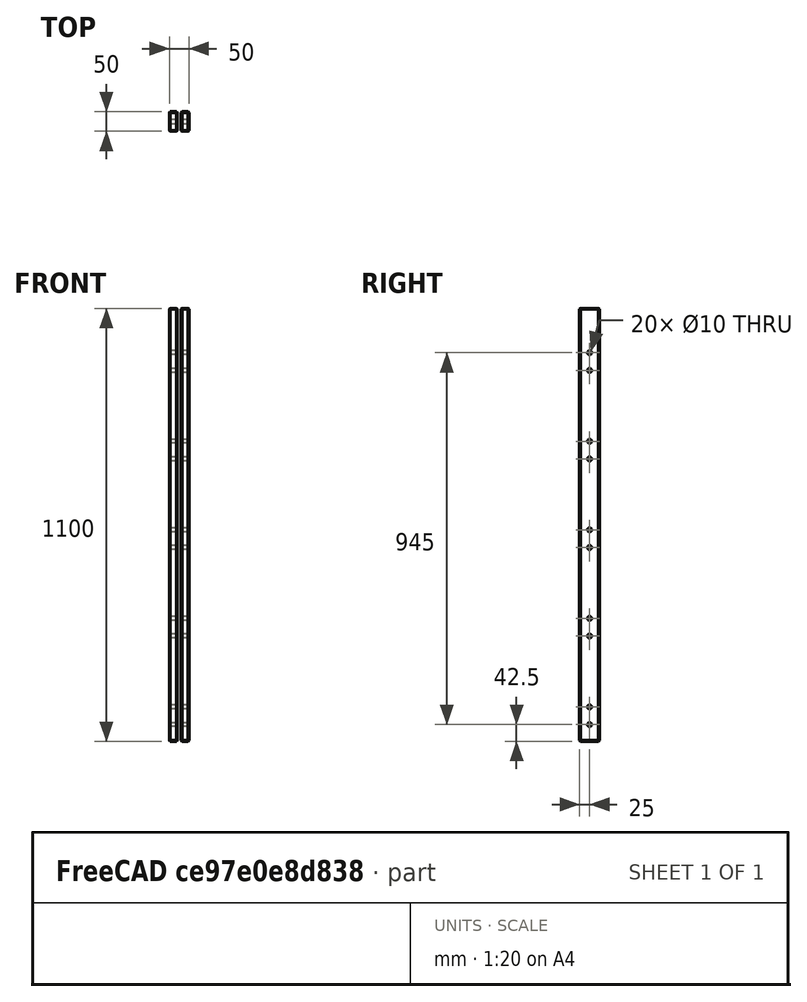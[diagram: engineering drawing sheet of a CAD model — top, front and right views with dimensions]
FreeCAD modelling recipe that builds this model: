
FCSTD DOCUMENT  (FreeCAD 0.17R10993 (Git))
Label: railing_wood
License: All rights reserved
LicenseURL: http://en.wikipedia.org/wiki/All_rights_reserved
objects: Part::Part2DObjectPython×22, Part::Feature×5, TechDraw::DrawProjGroupItem×3, Part::FeaturePython×2, Part::Box×1, Part::Mirroring×1, Part::Compound×1, Part::Chamfer×1, Part::Extrusion×1, Part::Cut×1, App::DocumentObjectGroup×1, TechDraw::DrawSVGTemplate×1, TechDraw::DrawProjGroup×1, TechDraw::DrawViewPart×1, TechDraw::DrawPage×1
note: 35 computed .brp shape members not serialized (recipe doc carries the construction recipe); baked Part::Feature solids carry a one-line shape summary decoded from their .brp

FEATURE [Part::Box] Box  label="Cube"
  AttacherType = Attacher::AttachEngine3D
  Height = 1100
  Length = 20
  Placement = pos=(-25,-23,-70) rot=(0,0,1;0rad)
  Width = 50
FEATURE [Part::Mirroring] mirror  label="Mirror of Cube"
  Base = (0,0,0)
  Normal = (1,0,0)
  Source = -> Box
FEATURE [Part::Compound] Compound
  Links = -> [mirror,Box]
  Placement = pos=(89.3902,-413,100) rot=(0,0,1;0rad)
FEATURE [Part::Chamfer] Chamfer  label="railing_wood"
  Base = -> Compound
  Edges = 24 edges r=2: [Edge1,Edge2,Edge3,Edge4,Edge5,Edge6,Edge7,Edge8,Edge9,Edge10,Edge11,Edge12,Edge13,Edge14,Edge15,Edge16,Edge17,Edge18,Edge19,Edge20,Edge21,Edge22,Edge23,Edge24]
FEATURE [Part::Feature] step_01_cs
  shape: bbox 1490 x 3e-07 x 1265 mm, 0 faces, 0 solids (baked)
FEATURE [Part::Feature] fridge_box_panels_01_cs
  shape: bbox 630 x 3e-07 x 2050 mm, 0 faces, 0 solids (baked)
FEATURE [Part::Part2DObjectPython] Line  # Draft 2D object (typed FeaturePython)
  ChamferSize = 0
  Closed = false
  End = (2100,-5,0)
  FilletRadius = 0
  Length = 2100.01
  MakeFace = true
  Points = (2) [(0,0,0),(2100,-5,0)]
  Start = (0,0,0)
  Subdivisions = 0
FEATURE [Part::Part2DObjectPython] Line002  # Draft 2D object (typed FeaturePython)
  ChamferSize = 0
  Closed = false
  End = (2900,0,2260)
  FilletRadius = 0
  Length = 800
  MakeFace = true
  Points = (2) [(2100,0,2260),(2900,0,2260)]
  Start = (2100,0,2260)
  Subdivisions = 0
FEATURE [Part::Part2DObjectPython] DWire  # Draft 2D object (typed FeaturePython)
  ChamferSize = 0
  Closed = false
  End = (2900,0,2105)
  FilletRadius = 0
  Length = 1755
  MakeFace = true
  Points = (4) [(2900,0,2260),(2100,0,2260),(2100,0,2105),(2900,0,2105)]
  Start = (2900,0,2260)
  Subdivisions = 0
FEATURE [Part::Part2DObjectPython] Line003  # Draft 2D object (typed FeaturePython)
  ChamferSize = 0
  Closed = false
  End = (2100,0,3260)
  FilletRadius = 0
  Length = 1000
  MakeFace = true
  Points = (2) [(2100,0,2260),(2100,0,3260)]
  Start = (2100,0,2260)
  Subdivisions = 0
FEATURE [Part::Part2DObjectPython] Line005  # Draft 2D object (typed FeaturePython)
  ChamferSize = 0
  Closed = false
  End = (0,0,1205)
  FilletRadius = 0
  Length = 1000
  MakeFace = true
  Points = (2) [(-1.18132e-16,0,205),(-1.18132e-16,0,1205)]
  Start = (0,0,205)
  Subdivisions = 0
FEATURE [Part::Part2DObjectPython] Line009  # Draft 2D object (typed FeaturePython)
  ChamferSize = 0
  Closed = false
  End = (89.3902,0,1222.39)
  FilletRadius = 0
  Length = 902.176
  MakeFace = true
  Placement = pos=(-630,0,-420.411) rot=(0,0,1;0rad)
  Points = (2) [(719.39,0,740.622),(719.39,0,1642.8)]
  Start = (89.3902,0,320.211)
  Subdivisions = 0
FEATURE [Part::Feature] double_beam_01_cs001
  Placement = pos=(0,365,0) rot=(0,0,1;0rad)
  shape: bbox 1510 x 3e-07 x 1687 mm, 0 faces, 0 solids (baked)
FEATURE [Part::Part2DObjectPython] Line016  # Draft 2D object (typed FeaturePython)
  ChamferSize = 0
  Closed = false
  End = (148.345,-431,590)
  FilletRadius = 0
  Length = 58.9552
  MakeFace = true
  Placement = pos=(2.73e-10,-431,59.7885) rot=(0,0,1;0rad)
  Points = (2) [(89.3902,0,530.211),(148.345,0,530.211)]
  Start = (89.3902,-431,590)
  Subdivisions = 0
FEATURE [Part::Part2DObjectPython] Line019  # Draft 2D object (typed FeaturePython)
  ChamferSize = 0
  Closed = false
  End = (148.345,-431,815)
  FilletRadius = 0
  Length = 58.9552
  MakeFace = true
  Placement = pos=(2.73e-10,-431,284.789) rot=(0,0,1;0rad)
  Points = (2) [(89.3902,0,530.211),(148.345,0,530.211)]
  Start = (89.3902,-431,815)
  Subdivisions = 0
FEATURE [Part::Part2DObjectPython] Line022  # Draft 2D object (typed FeaturePython)
  ChamferSize = 0
  Closed = false
  End = (1490,0,1687.47)
  FilletRadius = 0
  Length = 2110.19
  MakeFace = true
  Points = (2) [(-20,0,213.426),(1490,0,1687.47)]
  Start = (-20,0,213.426)
  Subdivisions = 0
FEATURE [Part::Part2DObjectPython] Line023  # Draft 2D object (typed FeaturePython)
  ChamferSize = 0
  Closed = false
  End = (1490,0,2659.52)
  FilletRadius = 0
  Length = 2110.19
  MakeFace = true
  Placement = pos=(0,0,972.05) rot=(0,0,1;0rad)
  Points = (2) [(-20,0,213.426),(1490,0,1687.47)]
  Start = (-20,0,1185.48)
  Subdivisions = 0
FEATURE [Part::Part2DObjectPython] Line024  # Draft 2D object (typed FeaturePython)
  ChamferSize = 0
  Closed = false
  End = (1524.93,0,2623.75)
  FilletRadius = 0
  Length = 2110.19
  MakeFace = true
  Points = (2) [(14.9268,0,1149.7),(1524.93,0,2623.75)]
  Start = (14.9268,0,1149.7)
  Subdivisions = 0
FEATURE [Part::Part2DObjectPython] Line026  # Draft 2D object (typed FeaturePython)
  ChamferSize = 0
  Closed = false
  End = (148.345,-431,1040)
  FilletRadius = 0
  Length = 58.9552
  MakeFace = true
  Placement = pos=(2.74e-10,-431,509.789) rot=(0,0,1;0rad)
  Points = (2) [(89.3902,0,530.211),(148.345,0,530.211)]
  Start = (89.3902,-431,1040)
  Subdivisions = 0
FEATURE [Part::Part2DObjectPython] Line033  # Draft 2D object (typed FeaturePython)
  ChamferSize = 0
  Closed = false
  End = (89.3902,-431,500)
  FilletRadius = 0
  Length = 58.9552
  MakeFace = true
  Placement = pos=(-58.9552,-431,-30.2115) rot=(0,0,1;0rad)
  Points = (2) [(89.3902,0,530.211),(148.345,0,530.211)]
  Start = (30.4351,-431,500)
  Subdivisions = 0
FEATURE [Part::Part2DObjectPython] Line034  # Draft 2D object (typed FeaturePython)
  ChamferSize = 0
  Closed = false
  End = (89.3902,-431,725)
  FilletRadius = 0
  Length = 58.9552
  MakeFace = true
  Placement = pos=(-58.9552,-431,194.789) rot=(0,0,1;0rad)
  Points = (2) [(89.3902,0,530.211),(148.345,0,530.211)]
  Start = (30.4351,-431,725)
  Subdivisions = 0
FEATURE [Part::Part2DObjectPython] Line035  # Draft 2D object (typed FeaturePython)
  ChamferSize = 0
  Closed = false
  End = (89.3902,-431,950)
  FilletRadius = 0
  Length = 58.9552
  MakeFace = true
  Placement = pos=(-58.9552,-431,419.789) rot=(0,0,1;0rad)
  Points = (2) [(89.3902,0,530.211),(148.345,0,530.211)]
  Start = (30.4351,-431,950)
  Subdivisions = 0
FEATURE [Part::Part2DObjectPython] Line036  # Draft 2D object (typed FeaturePython)
  ChamferSize = 0
  Closed = false
  End = (148.345,-431,365)
  FilletRadius = 0
  Length = 58.9552
  MakeFace = true
  Placement = pos=(2.73e-10,-431,-165.211) rot=(0,0,1;0rad)
  Points = (2) [(89.3902,0,530.211),(148.345,0,530.211)]
  Start = (89.3902,-431,365)
  Subdivisions = 0
FEATURE [Part::Part2DObjectPython] Line037  # Draft 2D object (typed FeaturePython)
  ChamferSize = 0
  Closed = false
  End = (89.3902,-431,275)
  FilletRadius = 0
  Length = 58.9552
  MakeFace = true
  Placement = pos=(-58.9552,-431,-255.211) rot=(0,0,1;0rad)
  Points = (2) [(89.3902,0,530.211),(148.345,0,530.211)]
  Start = (30.4351,-431,275)
  Subdivisions = 0
FEATURE [Part::Part2DObjectPython] Line038  # Draft 2D object (typed FeaturePython)
  ChamferSize = 0
  Closed = false
  End = (89.3902,-431,50)
  FilletRadius = 0
  Length = 58.9552
  MakeFace = true
  Placement = pos=(-58.9552,-431,-480.211) rot=(0,0,1;0rad)
  Points = (2) [(89.3902,0,530.211),(148.345,0,530.211)]
  Start = (30.4351,-431,50)
  Subdivisions = 0
FEATURE [Part::Part2DObjectPython] Line039  # Draft 2D object (typed FeaturePython)
  ChamferSize = 0
  Closed = false
  End = (148.345,-431,140)
  FilletRadius = 0
  Length = 58.9552
  MakeFace = true
  Placement = pos=(2.73e-10,-431,-390.211) rot=(0,0,1;0rad)
  Points = (2) [(89.3902,0,530.211),(148.345,0,530.211)]
  Start = (89.3902,-431,140)
  Subdivisions = 0
FEATURE [Part::Part2DObjectPython] Circle  # Draft 2D object (typed FeaturePython)
  FirstAngle = 0
  LastAngle = 0
  MakeFace = true
  Placement = pos=(64.3902,-411,100) rot=(0.57735,-0.57735,-0.57735;2.0944rad)
  Radius = 5
  Support = -> [Chamfer]
FEATURE [Part::Extrusion] Extrude
  Base = -> Circle
  Dir = (1,0,0)
  DirMode = 0
  FaceMakerClass = Part::FaceMakerBullseye
  LengthFwd = 80
  LengthRev = 0
  Placement = pos=(25,0,0) rot=(0,0,1;0rad)
  Solid = false
  Symmetric = true
FEATURE [Part::FeaturePython] Array  # Draft array (typed FeaturePython)
  Angle = 360
  ArrayType = 0
  Axis = (0,0,1)
  Base = -> Extrude
  Center = (0,0,0)
  Fuse = false
  IntervalAxis = (0,0,0)
  IntervalX = (0,0,45)
  IntervalY = (0,0,225)
  IntervalZ = (0,0,0)
  NumberPolar = 1
  NumberX = 2
  NumberY = 5
  NumberZ = 1
  Placement = pos=(0,0,-27.5) rot=(0,0,1;0rad)
FEATURE [Part::Cut] Cut  label="cutted_railing_wood"
  Base = -> Chamfer
  Tool = -> Array
FEATURE [Part::Feature] handrail_01_cs
  shape: bbox 2177 x 1e-05 x 2127 mm, 0 faces, 0 solids (baked)
FEATURE [Part::Feature] Cut_cs
  shape: bbox 50 x 3e-07 x 1100 mm, 0 faces, 0 solids (baked)
FEATURE [Part::Part2DObjectPython] Line043  # Draft 2D object (typed FeaturePython)
  ChamferSize = 0
  Closed = false
  End = (2157.46,-9.99981,3249.6)
  FilletRadius = 0
  Length = 3000
  MakeFace = true
  Points = (2) [(10.7356,-9.99993,1153.99),(2157.46,-9.99981,3249.6)]
  Start = (10.7356,-9.99993,1153.99)
  Subdivisions = 0
FEATURE [Part::Part2DObjectPython] Line044  # Draft 2D object (typed FeaturePython)
  ChamferSize = 0
  Closed = false
  End = (129.39,0,972.5)
  FilletRadius = 0
  Length = 80
  MakeFace = true
  Points = (2) [(49.3902,0,972.5),(129.39,0,972.5)]
  Start = (49.3902,0,972.5)
  Subdivisions = 0
FEATURE [App::DocumentObjectGroup] Group  label="drawing"
  Group = -> [step_01_cs,fridge_box_panels_01_cs,Line,Line002,DWire,Line003,Line005,Line009,double_beam_01_cs001,Line016,Line019,Line022,Line023,Line024,Line026,Line033,Line034,Line035,Line036,Line037,Line038,Line039,Line043,Cut_cs,handrail_01_cs,Line044]
FEATURE [Part::FeaturePython] Panel  # WARN: FeaturePython — macro-defined, semantics opaque (R4)
  Area = 0
  Base = -> Cut
  FaceMaker = 0
  HorizontalArea = 0
  Length = 0
  MoveWithHost = false
  Normal = (0,0,0)
  PerimeterLength = 0
  Role = 0
  Sheets = 1
  Thickness = 10
  VerticalArea = 0
  WaveDirection = 0
  WaveHeight = 0
  WaveLength = 0
  WaveType = 0
  Width = 0
FEATURE [TechDraw::DrawSVGTemplate] Template
  Height = 841
  Orientation = 0
  Width = 594
FEATURE [TechDraw::DrawProjGroupItem] ProjItem  label="Front"
  ArcCenterMarks = true
  CenterScale = 2
  Direction = (0,-1,0)
  HardHidden = true
  HiddenWidth = 0.15
  HorizCenterLine = false
  IsoCount = 0
  IsoHidden = false
  IsoVisible = false
  IsoWidth = 0.3
  KeepLabel = false
  LineWidth = 0.7
  Rotation = 0
  RotationVector = (1,0,0)
  Scale = 0.5
  ScaleType = 2
  SeamHidden = false
  SeamVisible = false
  ShowSectionLine = true
  SmoothHidden = false
  SmoothVisible = false
  Source = -> Panel
  Type = 0
  VertCenterLine = false
  X = 255.642
  Y = -221.426
FEATURE [TechDraw::DrawProjGroupItem] ProjItem001  label="Left"
  ArcCenterMarks = true
  CenterScale = 2
  Direction = (-1,0,0)
  HardHidden = true
  HiddenWidth = 0.15
  HorizCenterLine = false
  IsoCount = 0
  IsoHidden = false
  IsoVisible = false
  IsoWidth = 0.3
  KeepLabel = false
  LineWidth = 0.7
  Rotation = 0
  RotationVector = (0,1,0)
  Scale = 0.5
  ScaleType = 2
  SeamHidden = false
  SeamVisible = false
  ShowSectionLine = true
  SmoothHidden = false
  SmoothVisible = false
  Source = -> Panel
  Type = 1
  VertCenterLine = false
  X = 62.6576
  Y = 0
FEATURE [TechDraw::DrawProjGroupItem] ProjItem002  label="Top"
  ArcCenterMarks = true
  CenterScale = 2
  Direction = (0,0,1)
  HardHidden = true
  HiddenWidth = 0.15
  HorizCenterLine = false
  IsoCount = 0
  IsoHidden = false
  IsoVisible = false
  IsoWidth = 0.3
  KeepLabel = false
  LineWidth = 0.7
  Rotation = 0
  RotationVector = (1,0,0)
  Scale = 0.5
  ScaleType = 2
  SeamHidden = false
  SeamVisible = false
  ShowSectionLine = true
  SmoothHidden = false
  SmoothVisible = false
  Source = -> Panel
  Type = 4
  VertCenterLine = false
  X = 0
  Y = -320.44
FEATURE [TechDraw::DrawProjGroup] ProjGroup
  Anchor = -> ProjItem
  AutoDistribute = true
  KeepLabel = false
  ProjectionType = 0
  Rotation = 0
  Scale = 0.5
  ScaleType = 2
  Source = -> Panel
  Views = -> [ProjItem,ProjItem001,ProjItem002]
  X = 110.108
  Y = 523.613
  spacingX = 25
  spacingY = 25
FEATURE [TechDraw::DrawViewPart] View
  ArcCenterMarks = true
  CenterScale = 2
  Direction = (-0.45,-1,0.5)
  HardHidden = true
  HiddenWidth = 0.15
  HorizCenterLine = false
  IsoCount = 0
  IsoHidden = false
  IsoVisible = false
  IsoWidth = 0.3
  KeepLabel = false
  LineWidth = 0.7
  Rotation = 0
  Scale = 0.5
  ScaleType = 2
  SeamHidden = false
  SeamVisible = false
  ShowSectionLine = true
  SmoothHidden = false
  SmoothVisible = false
  Source = -> Panel
  VertCenterLine = false
  X = 297
  Y = 420.5
FEATURE [TechDraw::DrawPage] Page
  ProjectionType = 0
  Template = -> Template
  Views = -> [ProjGroup,View]
